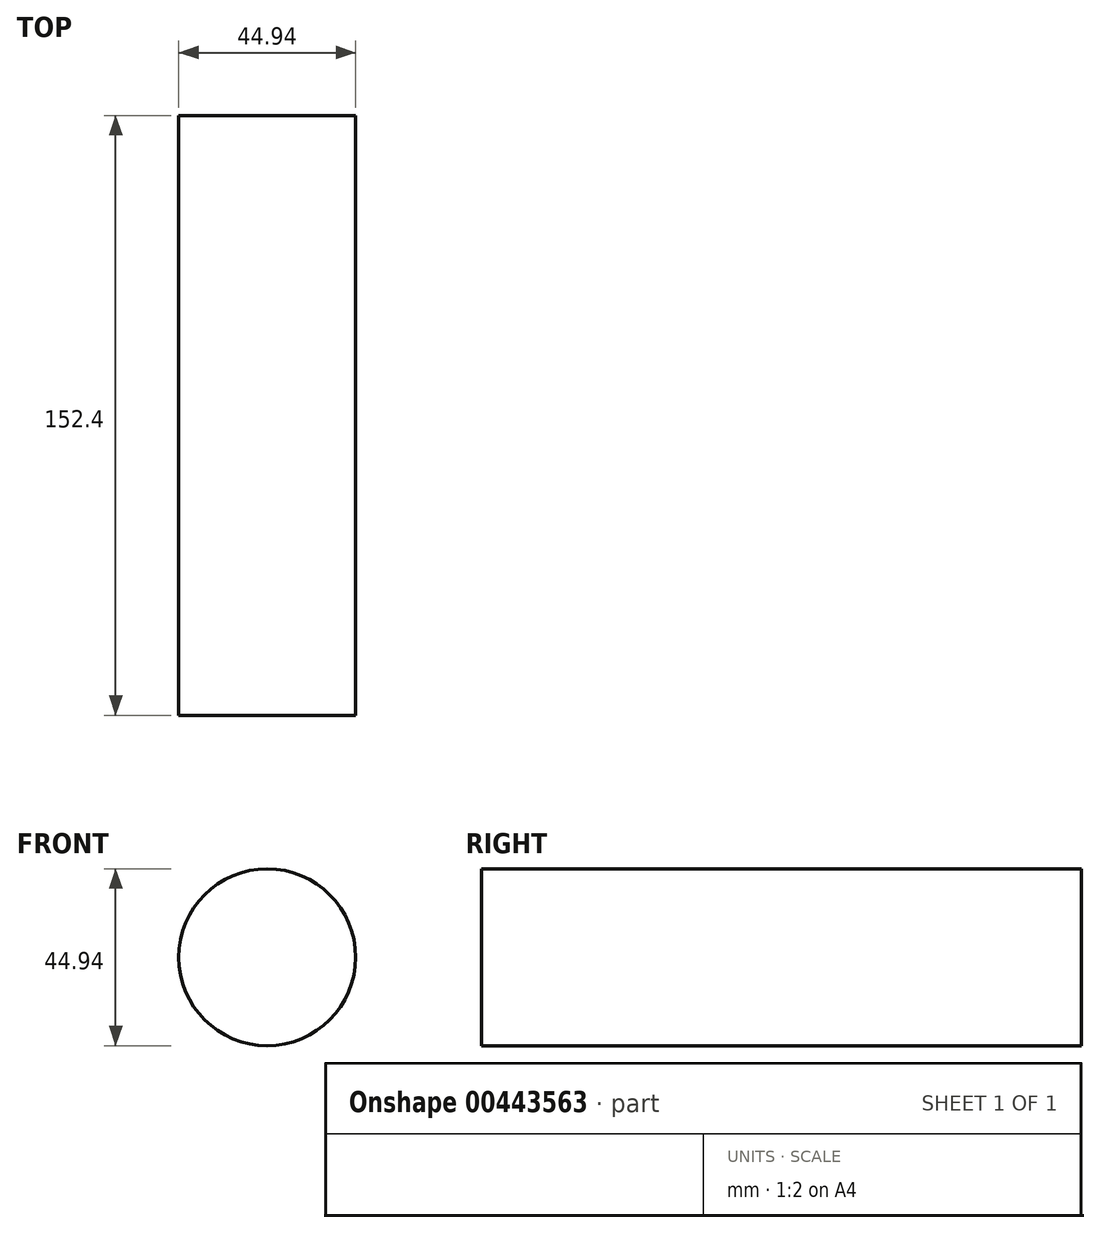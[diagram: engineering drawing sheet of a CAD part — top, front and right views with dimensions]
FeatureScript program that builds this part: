
annotation { "Feature Type Name" : "Feature", "Feature Type Description" : "" }
export const myFeature = defineFeature(function(context is Context, id is Id, definition is map)
    precondition{}
    {
        {
            var Q0;
            Q0=qCreatedBy(makeId("Front.planeOp"),FACE);
            var sketch = newSketch(context, id + "F0", { "sketchPlane" : qUnion([Q0])});
            skCircle(sketch, "E0", {"center": v(0, 0) * mm, "radius": 22.47 * mm});
            skSolve(sketch);
        }
        {
            var Q0;
            Q0=sQuery(id+"F0.wireOp",EDGE,"E0");
            extrude(context, id + "F1", {"bodyType" : ToolBodyType.SURFACE, "surfaceEntities" : qUnion([Q0]), "depth" : 152.4 * mm});
        }
    });
